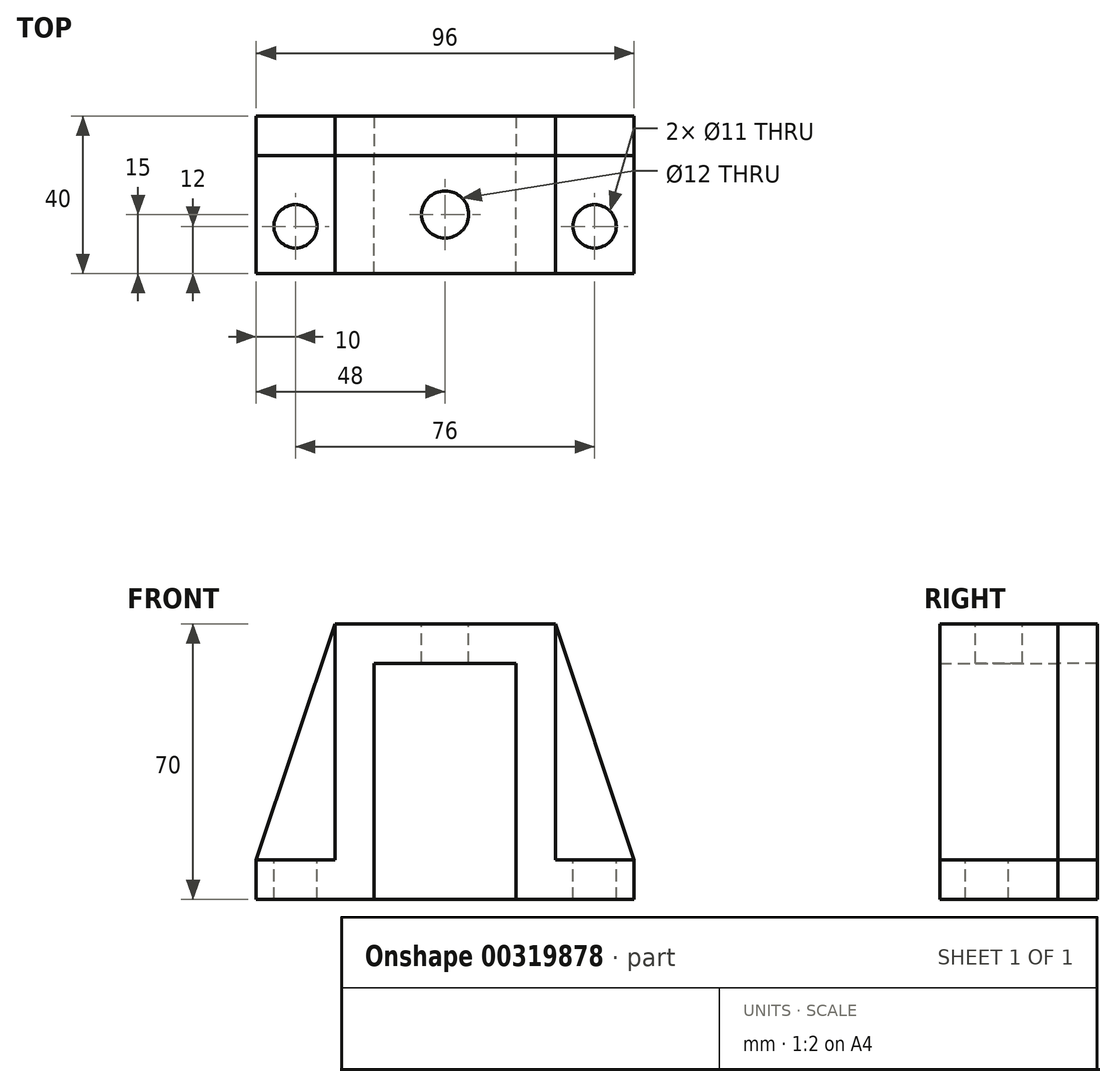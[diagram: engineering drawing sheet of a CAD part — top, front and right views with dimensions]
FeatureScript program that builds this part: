
annotation { "Feature Type Name" : "Feature", "Feature Type Description" : "" }
export const myFeature = defineFeature(function(context is Context, id is Id, definition is map)
    precondition{}
    {
        {
            var Q0;
            Q0=qCreatedBy(makeId("Front.planeOp"),FACE);
            var sketch = newSketch(context, id + "F0", { "sketchPlane" : qUnion([Q0])});
            skLineSegment(sketch, "E0", {"start": v(-48, -10) * mm, "end": v(-48, -20) * mm});
            skLineSegment(sketch, "E1", {"start": v(-48, -20) * mm, "end": v(-18, -20) * mm});
            skLineSegment(sketch, "E2", {"start": v(-18, -20) * mm, "end": v(-18, 40) * mm});
            skLineSegment(sketch, "E3", {"start": v(-18, 40) * mm, "end": v(18, 40) * mm});
            skLineSegment(sketch, "E4", {"start": v(18, 40) * mm, "end": v(18, -20) * mm});
            skLineSegment(sketch, "E5", {"start": v(18, -20) * mm, "end": v(48, -20) * mm});
            skLineSegment(sketch, "E6", {"start": v(48, -20) * mm, "end": v(48, -10) * mm});
            skLineSegment(sketch, "E7", {"start": v(48, -10) * mm, "end": v(28, -10) * mm});
            skLineSegment(sketch, "E8", {"start": v(28, -10) * mm, "end": v(28, 50) * mm});
            skLineSegment(sketch, "E9", {"start": v(28, 50) * mm, "end": v(-28, 50) * mm});
            skLineSegment(sketch, "E10", {"start": v(-28, 50) * mm, "end": v(-28, -10) * mm});
            skLineSegment(sketch, "E11", {"start": v(-28, -10) * mm, "end": v(-48, -10) * mm});
            skSolve(sketch);
        }
        {
            var Q0;
            Q0=makeQuery(id+"F0.imprint","IMPRINT",FACE,{"disambiguationData":[TD([[makeQuery(id+"F0.imprint","IMPRINT",EDGE,{"derivedFrom":sQuery(id+"F0.wireOp",EDGE,"E0")}),1.0]])]});
            extrude(context, id + "F1", {"entities" : qUnion([Q0]), "depth" : 30 * mm});
        }
        {
            var Q0;
            Q0=makeQuery(id+"F1.opExtrude","CAP_FACE",FACE,{"disambiguationData":[OSD([sQuery(id+"F0.wireOp",EDGE,"E0"),sQuery(id+"F0.wireOp",EDGE,"E1"),sQuery(id+"F0.wireOp",EDGE,"E2"),sQuery(id+"F0.wireOp",EDGE,"E3"),sQuery(id+"F0.wireOp",EDGE,"E4"),sQuery(id+"F0.wireOp",EDGE,"E5"),sQuery(id+"F0.wireOp",EDGE,"E6"),sQuery(id+"F0.wireOp",EDGE,"E7"),sQuery(id+"F0.wireOp",EDGE,"E8"),sQuery(id+"F0.wireOp",EDGE,"E9"),sQuery(id+"F0.wireOp",EDGE,"E10"),sQuery(id+"F0.wireOp",EDGE,"E11")])],"isStart":true});
            var sketch = newSketch(context, id + "F2", { "sketchPlane" : qUnion([Q0])});
            skLineSegment(sketch, "E12", {"start": v(-28, 50) * mm, "end": v(-48, -10) * mm});
            skLineSegment(sketch, "E13", {"start": v(28, 50) * mm, "end": v(48, -10) * mm});
            skLineSegment(sketch, "E14", {"start": v(-18, -20) * mm, "end": v(18, -20) * mm});
            skLineSegment(sketch, "E15", {"start": v(18, -20) * mm, "end": v(18, 40) * mm});
            skLineSegment(sketch, "E16", {"start": v(18, 40) * mm, "end": v(-18, 40) * mm});
            skLineSegment(sketch, "E17", {"start": v(-18, 40) * mm, "end": v(-18, -20) * mm});
            skLineSegment(sketch, "E18", {"start": v(-48, -10) * mm, "end": v(-28, -10) * mm});
            skLineSegment(sketch, "E19", {"start": v(-28, -10) * mm, "end": v(-28, 50) * mm});
            skLineSegment(sketch, "E20", {"start": v(28, 50) * mm, "end": v(28, -10) * mm});
            skLineSegment(sketch, "E21", {"start": v(28, -10) * mm, "end": v(48, -10) * mm});
            skSolve(sketch);
        }
        {
            var Q0;
            Q0=makeQuery(id+"F2.imprint","IMPRINT",FACE,{"disambiguationData":[TD([[makeQuery(id+"F2.imprint","IMPRINT",EDGE,{"derivedFrom":sQuery(id+"F2.wireOp",EDGE,"E12")}),1.0]])]});
            var Q1;
            Q1=makeQuery(id+"F2.imprint","IMPRINT",FACE,{"disambiguationData":[TD([[makeQuery(id+"F2.imprint","IMPRINT",EDGE,{"derivedFrom":sQuery(id+"F2.wireOp",EDGE,"E13")}),-1.0]])]});
            extrude(context, id + "F3", {"entities" : qUnion([Q0, Q1]), "operationType" : NewBodyOperationType.ADD, "depth" : 10 * mm});
        }
        {
            var Q0;
            Q0=makeQuery(id+"F3.boolean.opBoolean","MERGE",FACE,{"derivedFrom":[makeQuery(id+"F1.opExtrude","CAP_FACE",FACE,{"disambiguationData":[OSD([sQuery(id+"F0.wireOp",EDGE,"E0"),sQuery(id+"F0.wireOp",EDGE,"E1"),sQuery(id+"F0.wireOp",EDGE,"E2"),sQuery(id+"F0.wireOp",EDGE,"E3"),sQuery(id+"F0.wireOp",EDGE,"E4"),sQuery(id+"F0.wireOp",EDGE,"E5"),sQuery(id+"F0.wireOp",EDGE,"E6"),sQuery(id+"F0.wireOp",EDGE,"E7"),sQuery(id+"F0.wireOp",EDGE,"E8"),sQuery(id+"F0.wireOp",EDGE,"E9"),sQuery(id+"F0.wireOp",EDGE,"E10"),sQuery(id+"F0.wireOp",EDGE,"E11")])],"isStart":true}),makeQuery(id+"F3.opExtrude","CAP_FACE",FACE,{"disambiguationData":[OSD([sQuery(id+"F2.wireOp",EDGE,"E12"),sQuery(id+"F2.wireOp",EDGE,"E18"),sQuery(id+"F2.wireOp",EDGE,"E19")])],"isStart":true}),makeQuery(id+"F3.opExtrude","CAP_FACE",FACE,{"disambiguationData":[OSD([sQuery(id+"F2.wireOp",EDGE,"E13"),sQuery(id+"F2.wireOp",EDGE,"E20"),sQuery(id+"F2.wireOp",EDGE,"E21")])],"isStart":true})]});
            var sketch = newSketch(context, id + "F4", { "sketchPlane" : qUnion([Q0])});
            skLineSegment(sketch, "E22", {"start": v(-18, 40) * mm, "end": v(18, 40) * mm});
            skLineSegment(sketch, "E23", {"start": v(18, 40) * mm, "end": v(18, -20) * mm});
            skLineSegment(sketch, "E24", {"start": v(18, -20) * mm, "end": v(-18, -20) * mm});
            skLineSegment(sketch, "E25", {"start": v(-18, -20) * mm, "end": v(-18, 40) * mm});
            skSolve(sketch);
        }
        {
            var Q0;
            Q0=makeQuery(id+"F4.imprint","IMPRINT",FACE,{"disambiguationData":[TD([[makeQuery(id+"F4.imprint","IMPRINT",EDGE,{"derivedFrom":sQuery(id+"F4.wireOp",EDGE,"E22")}),1.0]])]});
            extrude(context, id + "F5", {"entities" : qUnion([Q0]), "depth" : 10 * mm});
        }
        {
            var Q0;
            Q0=makeQuery(id+"F1.opExtrude","SWEPT_FACE",FACE,{"disambiguationData":[OSD([sQuery(id+"F0.wireOp",EDGE,"E11")])]});
            var sketch = newSketch(context, id + "F6", { "sketchPlane" : qUnion([Q0])});
            skCircle(sketch, "E26", {"center": v(-38, -18) * mm, "radius": 5.5 * mm});
            skSolve(sketch);
        }
        {
            var Q0;
            Q0=makeQuery(id+"F6.imprint","IMPRINT",FACE,{"disambiguationData":[TD([[makeQuery(id+"F6.imprint","IMPRINT",EDGE,{"derivedFrom":sQuery(id+"F6.wireOp",EDGE,"E26")}),1.0]])]});
            extrude(context, id + "F7", {"entities" : qUnion([Q0]), "operationType" : NewBodyOperationType.REMOVE, "oppositeDirection" : true, "depth" : 25 * mm});
        }
        {
            var Q0;
            Q0=makeQuery(id+"F1.opExtrude","CAP_FACE",FACE,{"disambiguationData":[OSD([sQuery(id+"F0.wireOp",EDGE,"E0"),sQuery(id+"F0.wireOp",EDGE,"E1"),sQuery(id+"F0.wireOp",EDGE,"E2"),sQuery(id+"F0.wireOp",EDGE,"E3"),sQuery(id+"F0.wireOp",EDGE,"E4"),sQuery(id+"F0.wireOp",EDGE,"E5"),sQuery(id+"F0.wireOp",EDGE,"E6"),sQuery(id+"F0.wireOp",EDGE,"E7"),sQuery(id+"F0.wireOp",EDGE,"E8"),sQuery(id+"F0.wireOp",EDGE,"E9"),sQuery(id+"F0.wireOp",EDGE,"E10"),sQuery(id+"F0.wireOp",EDGE,"E11")])],"isStart":true});
            var sketch = newSketch(context, id + "F8", { "sketchPlane" : qUnion([Q0])});
            skLineSegment(sketch, "E27", {"start": v(-28, 50) * mm, "end": v(-28, -10) * mm});
            skLineSegment(sketch, "E28", {"start": v(-28, -10) * mm, "end": v(-48, -10) * mm});
            skLineSegment(sketch, "E29", {"start": v(-48, -10) * mm, "end": v(-48, -20) * mm});
            skLineSegment(sketch, "E30", {"start": v(-48, -20) * mm, "end": v(-18, -20) * mm});
            skLineSegment(sketch, "E31", {"start": v(-18, -20) * mm, "end": v(-18, 40) * mm});
            skLineSegment(sketch, "E32", {"start": v(-18, 40) * mm, "end": v(18, 40) * mm});
            skLineSegment(sketch, "E33", {"start": v(18, 40) * mm, "end": v(18, -20) * mm});
            skLineSegment(sketch, "E34", {"start": v(18, -20) * mm, "end": v(48, -20) * mm});
            skLineSegment(sketch, "E35", {"start": v(48, -20) * mm, "end": v(48, -10) * mm});
            skLineSegment(sketch, "E36", {"start": v(48, -10) * mm, "end": v(28, -10) * mm});
            skLineSegment(sketch, "E37", {"start": v(28, -10) * mm, "end": v(28, 50) * mm});
            skLineSegment(sketch, "E38", {"start": v(28, 50) * mm, "end": v(-28, 50) * mm});
            skSolve(sketch);
        }
        {
            var Q0;
            Q0=makeQuery(id+"F8.imprint","IMPRINT",FACE,{"disambiguationData":[TD([[makeQuery(id+"F8.imprint","IMPRINT",EDGE,{"derivedFrom":sQuery(id+"F8.wireOp",EDGE,"E27")}),-1.0]])]});
            extrude(context, id + "F9", {"entities" : qUnion([Q0]), "depth" : 10 * mm});
        }
        {
            var Q0;
            Q0=makeQuery(id+"F1.opExtrude","SWEPT_FACE",FACE,{"disambiguationData":[OSD([sQuery(id+"F0.wireOp",EDGE,"E7")])]});
            var sketch = newSketch(context, id + "F10", { "sketchPlane" : qUnion([Q0])});
            skCircle(sketch, "E39", {"center": v(38, -18) * mm, "radius": 5.5 * mm});
            skSolve(sketch);
        }
        {
            var Q0;
            Q0=makeQuery(id+"F10.imprint","IMPRINT",FACE,{"disambiguationData":[TD([[makeQuery(id+"F10.imprint","IMPRINT",EDGE,{"derivedFrom":sQuery(id+"F10.wireOp",EDGE,"E39")}),1.0]])]});
            var Q1;
            Q1=sQuery(id+"F10.wireOp",EDGE,"E39");
            extrude(context, id + "F11", {"entities" : qUnion([Q0]), "operationType" : NewBodyOperationType.REMOVE, "surfaceEntities" : qUnion([Q1]), "oppositeDirection" : true, "depth" : 25 * mm});
        }
        {
            var Q0;
            Q0=makeQuery(id+"F9.opExtrude","SWEPT_FACE",FACE,{"disambiguationData":[OSD([sQuery(id+"F8.wireOp",EDGE,"E38")])]});
            var sketch = newSketch(context, id + "F12", { "sketchPlane" : qUnion([Q0])});
            skCircle(sketch, "E40", {"center": v(0, -15) * mm, "radius": 6 * mm});
            skSolve(sketch);
        }
        {
            var Q0;
            Q0=makeQuery(id+"F12.imprint","IMPRINT",FACE,{"disambiguationData":[TD([[makeQuery(id+"F12.imprint","IMPRINT",EDGE,{"derivedFrom":sQuery(id+"F12.wireOp",EDGE,"E40")}),1.0]])]});
            extrude(context, id + "F13", {"entities" : qUnion([Q0]), "operationType" : NewBodyOperationType.REMOVE, "oppositeDirection" : true, "depth" : 25 * mm});
        }
    });
